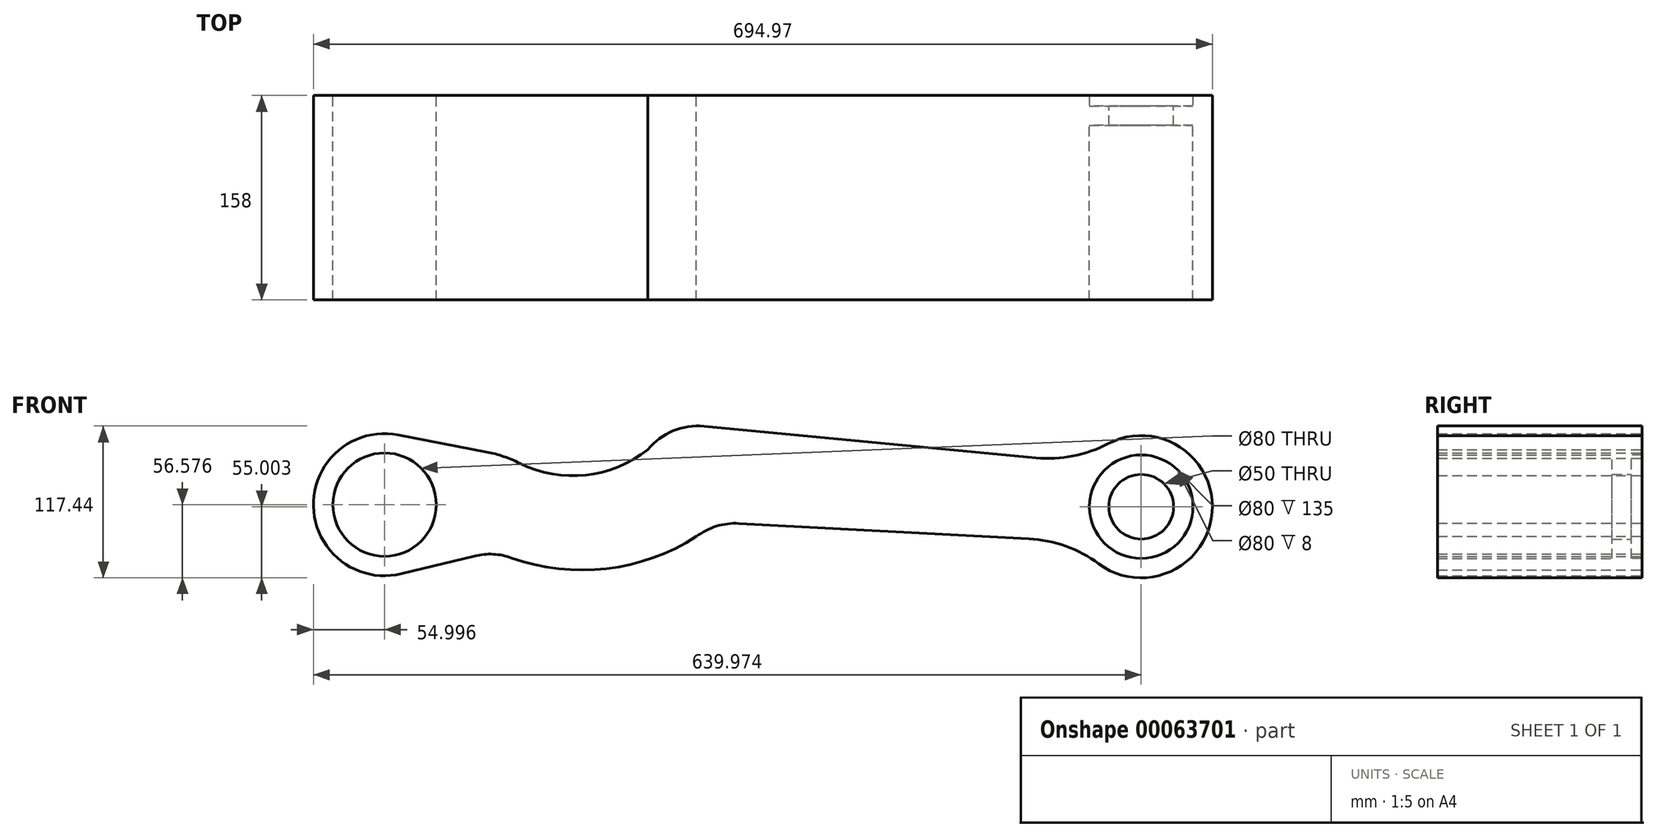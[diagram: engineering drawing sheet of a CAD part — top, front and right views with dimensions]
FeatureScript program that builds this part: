
annotation { "Feature Type Name" : "Feature", "Feature Type Description" : "" }
export const myFeature = defineFeature(function(context is Context, id is Id, definition is map)
    precondition{}
    {
        {
            var Q0;
            Q0=qCreatedBy(makeId("Front.planeOp"),FACE);
            var sketch = newSketch(context, id + "F0", { "sketchPlane" : qUnion([Q0])});
            skCircle(sketch, "E0", {"center": v(617.42, 352.56) * mm, "radius": 22.5 * mm});
            skCircle(sketch, "E1", {"center": v(32.45, 354.14) * mm, "radius": 22.5 * mm});
            skCircle(sketch, "E2", {"center": v(617.42, 352.56) * mm, "radius": 40 * mm});
            skCircle(sketch, "E3", {"center": v(32.45, 354.14) * mm, "radius": 40 * mm});
            skCircle(sketch, "E4", {"center": v(617.42, 352.56) * mm, "radius": 25 * mm});
            skCircle(sketch, "E5", {"center": v(32.45, 354.14) * mm, "radius": 25 * mm});
            skLineSegment(sketch, "E6", {"start": v(111.44, 394.84) * mm, "end": v(42.92, 408.13) * mm});
            skArc(sketch, "E7", {"start": v(42.92, 408.13) * mm, "mid": v(-22.54, 352.85) * mm, "end": v(45.42, 300.69) * mm});
            skLineSegment(sketch, "E8", {"start": v(45.42, 300.69) * mm, "end": v(102.16, 314.46) * mm});
            skArc(sketch, "E9", {"start": v(102.16, 314.46) * mm, "mid": v(116.53, 315.8) * mm, "end": v(130.69, 313) * mm});
            skArc(sketch, "E10", {"start": v(130.69, 313) * mm, "mid": v(204.06, 304.67) * mm, "end": v(273.59, 329.52) * mm});
            skArc(sketch, "E11", {"start": v(273.59, 329.52) * mm, "mid": v(289.14, 337.5) * mm, "end": v(306.48, 339.64) * mm});
            skLineSegment(sketch, "E12", {"start": v(306.48, 339.64) * mm, "end": v(530.55, 327.8) * mm});
            skArc(sketch, "E13", {"start": v(530.55, 327.8) * mm, "mid": v(559.07, 322.05) * mm, "end": v(584.72, 308.34) * mm});
            skArc(sketch, "E14", {"start": v(584.72, 308.34) * mm, "mid": v(672.26, 348.31) * mm, "end": v(591.93, 401.3) * mm});
            skArc(sketch, "E15", {"start": v(591.93, 401.3) * mm, "mid": v(564.8, 391.77) * mm, "end": v(536.1, 390.35) * mm});
            skLineSegment(sketch, "E16", {"start": v(536.1, 390.35) * mm, "end": v(279.38, 414.77) * mm});
            skArc(sketch, "E17", {"start": v(279.38, 414.77) * mm, "mid": v(255.47, 411.17) * mm, "end": v(236.05, 396.78) * mm});
            skArc(sketch, "E18", {"start": v(236.05, 396.78) * mm, "mid": v(188.02, 377.04) * mm, "end": v(136.92, 386.21) * mm});
            skArc(sketch, "E19", {"start": v(136.92, 386.21) * mm, "mid": v(124.47, 391.39) * mm, "end": v(111.44, 394.84) * mm});
            skSolve(sketch);
        }
        {
            var Q0;
            Q0 = qSketchRegion(id + "F0", true);
            var Q1;
            Q1=makeQuery(id+"F0.imprint","IMPRINT",FACE,{"disambiguationData":[TD([[makeQuery(id+"F0.imprint","IMPRINT",EDGE,{"derivedFrom":sQuery(id+"F0.wireOp",EDGE,"E2")}),1.0]])]});
            extrude(context, id + "F1", {"entities" : qUnion([Q0, Q1]), "depth" : 15 * mm});
        }
        {
            var Q0;
            Q0=makeQuery(id+"F0.imprint","IMPRINT",FACE,{"disambiguationData":[TD([[makeQuery(id+"F0.imprint","IMPRINT",EDGE,{"derivedFrom":sQuery(id+"F0.wireOp",EDGE,"E3")}),-1.0]])]});
            var Q1;
            Q1=sQuery(id+"F0.wireOp",EDGE,"E3");
            var Q2;
            Q2=sQuery(id+"F0.wireOp",EDGE,"E5");
            extrude(context, id + "F2", {"entities" : qUnion([Q0]), "operationType" : NewBodyOperationType.ADD, "surfaceEntities" : qUnion([Q1, Q2]), "depth" : 150 * mm});
        }
        {
            var Q0;
            Q0=makeQuery(id+"F0.imprint","IMPRINT",FACE,{"disambiguationData":[TD([[makeQuery(id+"F0.imprint","IMPRINT",EDGE,{"derivedFrom":sQuery(id+"F0.wireOp",EDGE,"E2")}),-1.0]])]});
            extrude(context, id + "F3", {"entities" : qUnion([Q0]), "operationType" : NewBodyOperationType.ADD, "depth" : 30 * mm});
        }
        {
            var Q0;
            Q0=makeQuery(id+"F0.imprint","IMPRINT",FACE,{"disambiguationData":[TD([[makeQuery(id+"F0.imprint","IMPRINT",EDGE,{"derivedFrom":sQuery(id+"F0.wireOp",EDGE,"E2")}),-1.0]])]});
            extrude(context, id + "F4", {"entities" : qUnion([Q0]), "operationType" : NewBodyOperationType.ADD, "oppositeDirection" : true, "depth" : 8 * mm});
        }
    });
